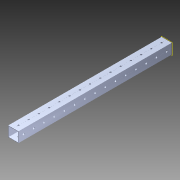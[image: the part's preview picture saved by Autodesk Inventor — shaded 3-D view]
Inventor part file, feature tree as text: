
AUTODESK INVENTOR PART (.ipt)
format: ipt  version: 2014 (Build 180170000, 170)  size: 1,198,592 bytes
history: native  units: in
note: dims shown in document units (in); Inventor stores cm internally (conversion verified against a paired STEP export)
features: pattern_circular x1, other x1, plane x1, extrude x1, imported_body x1, sketch x1
ambient origin geometry x8: Origin, YZ Plane, XZ Plane, XY Plane, X Axis, Y Axis, Z Axis, Center Point
bodies: Body1 (feature_tree)
feature tree (6):
  pattern_circular  "CirPattern2"
  other  "217-3426-STEP1"
  plane  "Work Plane1"
  extrude  "Extrusion1"  Depth=3937.0079in TaperAngle=0.0deg
  imported_body  "Base1"
  sketch  "Sketch1"  dims[d0=-15.0in d1=3937.0079in d2=0.0in]
